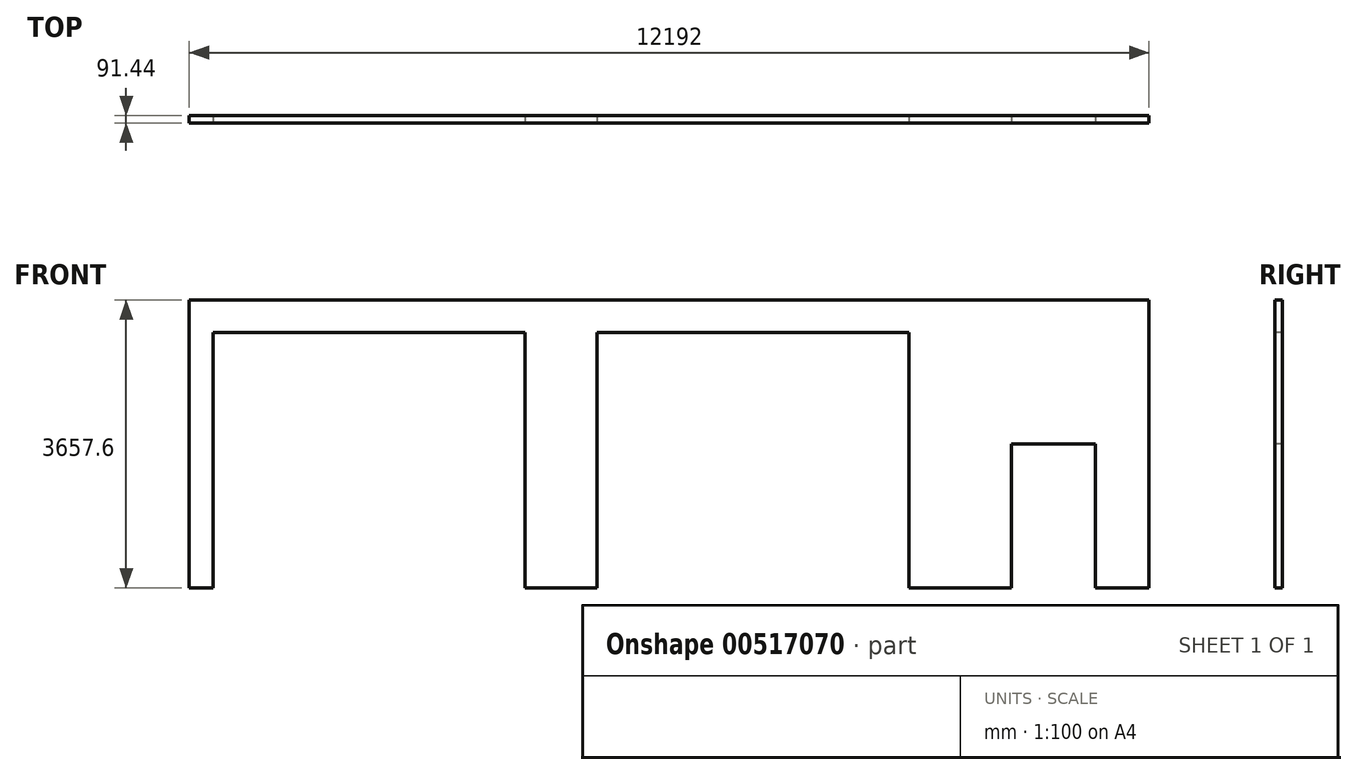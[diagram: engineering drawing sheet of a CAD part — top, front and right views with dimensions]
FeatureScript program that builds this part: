
annotation { "Feature Type Name" : "Feature", "Feature Type Description" : "" }
export const myFeature = defineFeature(function(context is Context, id is Id, definition is map)
    precondition{}
    {
        {
            var Q0;
            Q0=qCreatedBy(makeId("Top.planeOp"),FACE);
            var sketch = newSketch(context, id + "F0", { "sketchPlane" : qUnion([Q0])});
            skLineSegment(sketch, "E0", {"start": v(-6127.8, -21.24) * mm, "end": v(6064.2, -21.24) * mm});
            skLineSegment(sketch, "E1", {"start": v(6064.2, -21.24) * mm, "end": v(6064.2, -112.68) * mm});
            skLineSegment(sketch, "E2", {"start": v(6064.2, -112.68) * mm, "end": v(-6127.8, -112.68) * mm});
            skLineSegment(sketch, "E3", {"start": v(-6127.8, -112.68) * mm, "end": v(-6127.8, -21.24) * mm});
            skSolve(sketch);
        }
        {
            var Q0;
            Q0=makeQuery(id+"F0.imprint","IMPRINT",FACE,{"disambiguationData":[TD([[makeQuery(id+"F0.imprint","IMPRINT",EDGE,{"derivedFrom":sQuery(id+"F0.wireOp",EDGE,"E0")}),-1.0]])]});
            extrude(context, id + "F1", {"entities" : qUnion([Q0]), "depth" : 3657.6 * mm, "offsetDistance" : 30.48 * mm});
        }
        {
            var Q0;
            Q0=makeQuery(id+"F1.opExtrude","SWEPT_FACE",FACE,{"disambiguationData":[OSD([sQuery(id+"F0.wireOp",EDGE,"E2")])]});
            var sketch = newSketch(context, id + "F2", { "sketchPlane" : qUnion([Q0])});
            skLineSegment(sketch, "E4", {"start": v(-6127.8, 0) * mm, "end": v(-5823, 0) * mm});
            skLineSegment(sketch, "E5", {"start": v(-5823, 0) * mm, "end": v(-1860.6, 0) * mm});
            skLineSegment(sketch, "E6", {"start": v(-5823, 0) * mm, "end": v(-5823, 3246.57) * mm});
            skLineSegment(sketch, "E7", {"start": v(-5823, 3246.57) * mm, "end": v(-1860.6, 3246.57) * mm});
            skLineSegment(sketch, "E8", {"start": v(-1860.6, 3246.57) * mm, "end": v(-1860.6, 0) * mm});
            skLineSegment(sketch, "E9", {"start": v(-1860.6, 0) * mm, "end": v(-946.2, 0) * mm});
            skLineSegment(sketch, "E10", {"start": v(-946.2, 0) * mm, "end": v(3016.2, 0) * mm});
            skLineSegment(sketch, "E11", {"start": v(-946.2, 0) * mm, "end": v(-946.2, 3246.57) * mm});
            skLineSegment(sketch, "E12", {"start": v(-946.2, 3246.57) * mm, "end": v(3016.2, 3246.57) * mm});
            skLineSegment(sketch, "E13", {"start": v(3016.2, 3246.57) * mm, "end": v(3016.2, 0) * mm});
            skLineSegment(sketch, "E14", {"start": v(5380.27, 0) * mm, "end": v(5380.27, 1828.8) * mm});
            skPoint(sketch, "E14.endSnap0", {"position": v(6064.2, 1828.8) * mm});
            skLineSegment(sketch, "E15", {"start": v(5380.27, 1828.8) * mm, "end": v(4313.47, 1828.8) * mm});
            skLineSegment(sketch, "E16", {"start": v(4313.47, 1828.8) * mm, "end": v(4313.47, 0) * mm});
            skLineSegment(sketch, "E17", {"start": v(4313.47, 0) * mm, "end": v(5380.27, 0) * mm});
            skSolve(sketch);
        }
        {
            var Q0;
            Q0=makeQuery(id+"F2.imprint","IMPRINT",FACE,{"disambiguationData":[TD([[makeQuery(id+"F2.imprint","IMPRINT",EDGE,{"derivedFrom":sQuery(id+"F2.wireOp",EDGE,"E10")}),-1.0]])]});
            extrude(context, id + "F3", {"entities" : qUnion([Q0]), "operationType" : NewBodyOperationType.REMOVE, "oppositeDirection" : true, "depth" : 1676.4 * mm, "offsetDistance" : 30.48 * mm});
        }
        {
            var Q0;
            Q0 = qSketchRegion(id + "F2", true);
            extrude(context, id + "F4", {"entities" : qUnion([Q0]), "operationType" : NewBodyOperationType.REMOVE, "oppositeDirection" : true, "depth" : 1862.33 * mm, "offsetDistance" : 30.48 * mm});
        }
    });
